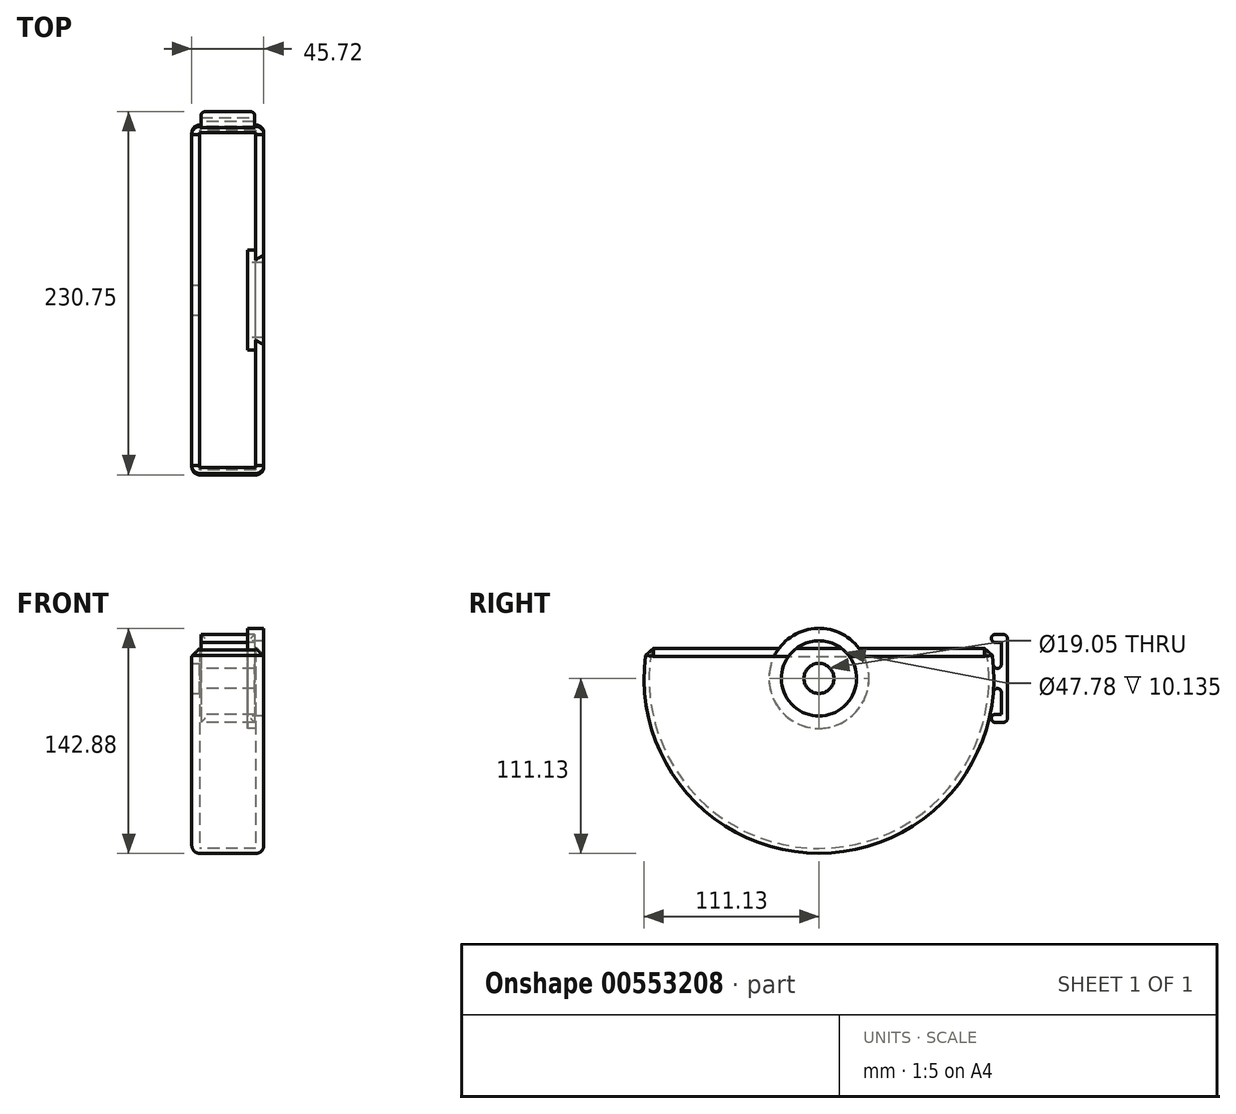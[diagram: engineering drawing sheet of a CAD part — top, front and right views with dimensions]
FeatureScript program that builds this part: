
annotation { "Feature Type Name" : "Feature", "Feature Type Description" : "" }
export const myFeature = defineFeature(function(context is Context, id is Id, definition is map)
    precondition{}
    {
        {
            var Q0;
            Q0=qCreatedBy(makeId("Right.planeOp"),FACE);
            var sketch = newSketch(context, id + "F0", { "sketchPlane" : qUnion([Q0])});
            skCircle(sketch, "E0", {"center": v(0, 0) * mm, "radius": 9.52 * mm});
            skSolve(sketch);
        }
        {
            var Q0;
            Q0=qCreatedBy(makeId("Right.planeOp"),FACE);
            var sketch = newSketch(context, id + "F1", { "sketchPlane" : qUnion([Q0])});
            skCircle(sketch, "E1", {"center": v(0, 0) * mm, "radius": 111.13 * mm});
            skCircle(sketch, "E2", {"center": v(0, 0) * mm, "radius": 107.95 * mm});
            skSolve(sketch);
        }
        {
            var Q0;
            Q0 = qSketchRegion(id + "F1", true);
            extrude(context, id + "F2", {"entities" : qUnion([Q0]), "endBound" : BoundingType.SYMMETRIC, "depth" : 35.56 * mm, "offsetDistance" : 25.4 * mm});
        }
        {
            var Q0;
            Q0=qCreatedBy(makeId("Right.planeOp"),FACE);
            cPlane(context, id + "F3", {"entities" : qUnion([Q0]), "cplaneType" : CPlaneType.OFFSET, "offset" : 17.78 * mm, "width" : 152.4 * mm, "height" : 152.4 * mm});
        }
        {
            var Q0;
            Q0=qCreatedBy(makeId("Right.planeOp"),FACE);
            cPlane(context, id + "F4", {"entities" : qUnion([Q0]), "cplaneType" : CPlaneType.OFFSET, "offset" : 17.78 * mm, "oppositeDirection" : true, "width" : 152.4 * mm, "height" : 152.4 * mm});
        }
        {
            var Q0;
            Q0=qCreatedBy(id+"F3.planeOp",FACE);
            var sketch = newSketch(context, id + "F5", { "sketchPlane" : qUnion([Q0])});
            skCircle(sketch, "E3", {"center": v(0, 0) * mm, "radius": 111.13 * mm});
            skSolve(sketch);
        }
        {
            var Q0;
            Q0 = qSketchRegion(id + "F5", true);
            extrude(context, id + "F6", {"entities" : qUnion([Q0]), "operationType" : NewBodyOperationType.ADD, "depth" : 5.08 * mm, "offsetDistance" : 25.4 * mm});
        }
        {
            var Q0;
            Q0=qCreatedBy(id+"F4.planeOp",FACE);
            var sketch = newSketch(context, id + "F7", { "sketchPlane" : qUnion([Q0])});
            skCircle(sketch, "E4", {"center": v(0, 0) * mm, "radius": 111.13 * mm});
            skSolve(sketch);
        }
        {
            var Q0;
            Q0 = qSketchRegion(id + "F7", true);
            extrude(context, id + "F8", {"entities" : qUnion([Q0]), "operationType" : NewBodyOperationType.ADD, "oppositeDirection" : true, "depth" : 5.08 * mm, "offsetDistance" : 25.4 * mm});
        }
        {
            var Q0;
            Q0=qCreatedBy(makeId("Right.planeOp"),FACE);
            var sketch = newSketch(context, id + "F9", { "sketchPlane" : qUnion([Q0])});
            skLineSegment(sketch, "E5.bottom", {"start": v(-117, 19.1) * mm, "end": v(123.15, 19.1) * mm});
            skLineSegment(sketch, "E5.top", {"start": v(-117, 115.3) * mm, "end": v(123.15, 115.3) * mm});
            skLineSegment(sketch, "E5.left", {"start": v(-117, 19.1) * mm, "end": v(-117, 115.3) * mm});
            skLineSegment(sketch, "E5.right", {"start": v(123.15, 19.1) * mm, "end": v(123.15, 115.3) * mm});
            skSolve(sketch);
        }
        {
            var Q0;
            Q0 = qSketchRegion(id + "F9", true);
            extrude(context, id + "F10", {"entities" : qUnion([Q0]), "operationType" : NewBodyOperationType.REMOVE, "endBound" : BoundingType.SYMMETRIC, "depth" : 76.2 * mm, "offsetDistance" : 25.4 * mm});
        }
        {
            var Q0;
            Q0 = qSketchRegion(id + "F0", true);
            extrude(context, id + "F11", {"entities" : qUnion([Q0]), "operationType" : NewBodyOperationType.REMOVE, "endBound" : BoundingType.SYMMETRIC, "oppositeDirection" : true, "depth" : 76.2 * mm, "offsetDistance" : 25.4 * mm});
        }
        {
            var Q0;
            Q0=makeQuery(id+"F8.opExtrude","CAP_EDGE",EDGE,{"disambiguationData":[OSD([sQuery(id+"F7.wireOp",EDGE,"E4")])],"isStart":false});
            var Q1;
            Q1=makeQuery(id+"F6.opExtrude","CAP_EDGE",EDGE,{"disambiguationData":[OSD([sQuery(id+"F5.wireOp",EDGE,"E3")])],"isStart":false});
            var Q2;
            Q2=makeQuery(id+"F2.opExtrude","CAP_EDGE",EDGE,{"disambiguationData":[OSD([sQuery(id+"F1.wireOp",EDGE,"E2")])],"isStart":true});
            var Q3;
            Q3=makeQuery(id+"F2.opExtrude","CAP_EDGE",EDGE,{"disambiguationData":[OSD([sQuery(id+"F1.wireOp",EDGE,"E2")])],"isStart":false});
            fillet(context, id + "F12", {"entities" : qUnion([Q0, Q1, Q2, Q3]), "radius" : 5.08 * mm, "tangentPropagation" : true, "allowEdgeOverflow" : false});
        }
        {
            var Q0;
            Q0=qCreatedBy(makeId("Right.planeOp"),FACE);
            var sketch = newSketch(context, id + "F13", { "sketchPlane" : qUnion([Q0])});
            skLineSegment(sketch, "E6.bottom", {"start": v(119.62, 27.94) * mm, "end": v(115.81, 27.94) * mm});
            skLineSegment(sketch, "E6.top", {"start": v(119.62, -27.94) * mm, "end": v(115.81, -27.94) * mm});
            skLineSegment(sketch, "E6.left", {"start": v(119.62, 27.94) * mm, "end": v(119.62, -27.94) * mm});
            skLineSegment(sketch, "E6.right", {"start": v(115.81, 27.94) * mm, "end": v(115.81, -27.94) * mm});
            skPoint(sketch, "E6.middle", {"position": v(117.72, 0) * mm});
            skLineSegment(sketch, "E7.bottom", {"start": v(110.33, -1.9) * mm, "end": v(119.12, -1.9) * mm});
            skLineSegment(sketch, "E7.top", {"start": v(110.33, 1.9) * mm, "end": v(119.12, 1.9) * mm});
            skLineSegment(sketch, "E7.left", {"start": v(110.33, -1.9) * mm, "end": v(110.33, 1.9) * mm});
            skLineSegment(sketch, "E7.right", {"start": v(119.12, -1.9) * mm, "end": v(119.12, 1.9) * mm});
            skLineSegment(sketch, "E8.bottom", {"start": v(115.81, 27.94) * mm, "end": v(109.46, 27.94) * mm});
            skLineSegment(sketch, "E8.top", {"start": v(115.81, 22.86) * mm, "end": v(109.46, 22.86) * mm});
            skLineSegment(sketch, "E8.left", {"start": v(115.81, 27.94) * mm, "end": v(115.81, 22.86) * mm});
            skLineSegment(sketch, "E8.right", {"start": v(109.46, 27.94) * mm, "end": v(109.46, 22.86) * mm});
            skLineSegment(sketch, "E9.bottom", {"start": v(115.81, -27.94) * mm, "end": v(109.46, -27.94) * mm});
            skLineSegment(sketch, "E9.top", {"start": v(115.81, -22.86) * mm, "end": v(109.46, -22.86) * mm});
            skLineSegment(sketch, "E9.left", {"start": v(115.81, -27.94) * mm, "end": v(115.81, -22.86) * mm});
            skLineSegment(sketch, "E9.right", {"start": v(109.46, -27.94) * mm, "end": v(109.46, -22.86) * mm});
            skSolve(sketch);
        }
        {
            var Q0;
            Q0 = qSketchRegion(id + "F13", true);
            extrude(context, id + "F14", {"entities" : qUnion([Q0]), "operationType" : NewBodyOperationType.ADD, "endBound" : BoundingType.SYMMETRIC, "depth" : 34.04 * mm, "offsetDistance" : 25.4 * mm});
        }
        {
            var Q0;
            Q0=makeQuery(id+"F14.boolean.opBoolean","INTERSECT",EDGE,{"derivedFrom":[makeQuery(id+"F8.boolean.opBoolean","MERGE",FACE,{"derivedFrom":[makeQuery(id+"F6.boolean.opBoolean","MERGE",FACE,{"derivedFrom":[makeQuery(id+"F2.opExtrude","SWEPT_FACE",FACE,{"disambiguationData":[OSD([sQuery(id+"F1.wireOp",EDGE,"E1")])]}),makeQuery(id+"F6.opExtrude","SWEPT_FACE",FACE,{"disambiguationData":[OSD([sQuery(id+"F5.wireOp",EDGE,"E3")])]})]}),makeQuery(id+"F8.opExtrude","SWEPT_FACE",FACE,{"disambiguationData":[OSD([sQuery(id+"F7.wireOp",EDGE,"E4")])]})]}),makeQuery(id+"F14.opExtrude","SWEPT_FACE",FACE,{"disambiguationData":[OSD([sQuery(id+"F13.wireOp",EDGE,"E7.top")])]})]});
            var Q1;
            Q1=makeQuery(id+"F14.boolean.opBoolean","INTERSECT",EDGE,{"derivedFrom":[makeQuery(id+"F8.boolean.opBoolean","MERGE",FACE,{"derivedFrom":[makeQuery(id+"F6.boolean.opBoolean","MERGE",FACE,{"derivedFrom":[makeQuery(id+"F2.opExtrude","SWEPT_FACE",FACE,{"disambiguationData":[OSD([sQuery(id+"F1.wireOp",EDGE,"E1")])]}),makeQuery(id+"F6.opExtrude","SWEPT_FACE",FACE,{"disambiguationData":[OSD([sQuery(id+"F5.wireOp",EDGE,"E3")])]})]}),makeQuery(id+"F8.opExtrude","SWEPT_FACE",FACE,{"disambiguationData":[OSD([sQuery(id+"F7.wireOp",EDGE,"E4")])]})]}),makeQuery(id+"F14.opExtrude","SWEPT_FACE",FACE,{"disambiguationData":[OSD([sQuery(id+"F13.wireOp",EDGE,"E7.bottom")])]})]});
            var Q2;
            Q2=makeQuery(id+"F14.opExtrude","SWEPT_EDGE",EDGE,{"disambiguationData":[OSD([sQuery(id+"F13.wireOp",EDGE,"E8.top"),sQuery(id+"F13.wireOp",EDGE,"E8.right")])]});
            var Q3;
            Q3=makeQuery(id+"F14.opExtrude","SWEPT_EDGE",EDGE,{"disambiguationData":[OSD([sQuery(id+"F13.wireOp",EDGE,"E9.bottom"),sQuery(id+"F13.wireOp",EDGE,"E9.right")])]});
            var Q4;
            Q4=makeQuery(id+"F14.opExtrude","SWEPT_EDGE",EDGE,{"disambiguationData":[OSD([sQuery(id+"F13.wireOp",EDGE,"E8.bottom"),sQuery(id+"F13.wireOp",EDGE,"E8.right")])]});
            var Q5;
            Q5=makeQuery(id+"F14.opExtrude","SWEPT_EDGE",EDGE,{"disambiguationData":[OSD([sQuery(id+"F13.wireOp",EDGE,"E9.top"),sQuery(id+"F13.wireOp",EDGE,"E9.right")])]});
            var Q6;
            Q6=makeQuery(id+"F14.opExtrude","SWEPT_EDGE",EDGE,{"disambiguationData":[OSD([sQuery(id+"F13.wireOp",EDGE,"E6.bottom"),sQuery(id+"F13.wireOp",EDGE,"E6.left")])]});
            var Q7;
            Q7=makeQuery(id+"F14.opExtrude","CAP_EDGE",EDGE,{"disambiguationData":[OSD([sQuery(id+"F13.wireOp",EDGE,"E6.left")])],"isStart":false});
            var Q8;
            Q8=makeQuery(id+"F14.opExtrude","CAP_EDGE",EDGE,{"disambiguationData":[OSD([sQuery(id+"F13.wireOp",EDGE,"E6.left")])],"isStart":true});
            var Q9;
            Q9=makeQuery(id+"F14.opExtrude","SWEPT_EDGE",EDGE,{"disambiguationData":[OSD([sQuery(id+"F13.wireOp",EDGE,"E6.top"),sQuery(id+"F13.wireOp",EDGE,"E6.left")])]});
            var Q10;
            Q10=makeQuery(id+"F14.opExtrude","SWEPT_EDGE",EDGE,{"disambiguationData":[OSD([sQuery(id+"F13.wireOp",EDGE,"E6.right"),sQuery(id+"F13.wireOp",EDGE,"E7.top")])]});
            var Q11;
            Q11=makeQuery(id+"F14.opExtrude","SWEPT_EDGE",EDGE,{"disambiguationData":[OSD([sQuery(id+"F13.wireOp",EDGE,"E6.right"),sQuery(id+"F13.wireOp",EDGE,"E7.bottom")])]});
            fillet(context, id + "F15", {"entities" : qUnion([Q0, Q1, Q2, Q3, Q4, Q5, Q6, Q7, Q8, Q9, Q10, Q11]), "radius" : 2.54 * mm, "tangentPropagation" : true, "allowEdgeOverflow" : false});
        }
        {
            var Q0;
            Q0=qCreatedBy(id+"F3.planeOp",FACE);
            var sketch = newSketch(context, id + "F16", { "sketchPlane" : qUnion([Q0])});
            skCircle(sketch, "E10", {"center": v(0, 0) * mm, "radius": 31.75 * mm});
            skSolve(sketch);
        }
        {
            var Q0;
            Q0 = qSketchRegion(id + "F16", true);
            extrude(context, id + "F17", {"entities" : qUnion([Q0]), "operationType" : NewBodyOperationType.ADD, "endBound" : BoundingType.SYMMETRIC, "depth" : 10.1 * mm, "offsetDistance" : 25.4 * mm});
        }
        {
            var Q0;
            Q0=qCreatedBy(makeId("Right.planeOp"),FACE);
            var sketch = newSketch(context, id + "F18", { "sketchPlane" : qUnion([Q0])});
            skCircle(sketch, "E11", {"center": v(0, 0) * mm, "radius": 23.89 * mm});
            skSolve(sketch);
        }
        {
            var Q0;
            Q0 = qSketchRegion(id + "F18", true);
            extrude(context, id + "F19", {"entities" : qUnion([Q0]), "operationType" : NewBodyOperationType.REMOVE, "depth" : 50.8 * mm, "offsetDistance" : 25.4 * mm});
        }
        {
            var Q0;
            Q0=qCreatedBy(makeId("Right.planeOp"),FACE);
            var sketch = newSketch(context, id + "F20", { "sketchPlane" : qUnion([Q0])});
            skLineSegment(sketch, "E12.bottom", {"start": v(116.97, 6.35) * mm, "end": v(110, 6.35) * mm});
            skLineSegment(sketch, "E12.top", {"start": v(116.97, -6.35) * mm, "end": v(110, -6.35) * mm});
            skLineSegment(sketch, "E12.left", {"start": v(116.97, 6.35) * mm, "end": v(116.97, -6.35) * mm});
            skLineSegment(sketch, "E12.right", {"start": v(110, 6.35) * mm, "end": v(110, -6.35) * mm});
            skPoint(sketch, "E12.middle", {"position": v(113.49, 0) * mm});
            skSolve(sketch);
        }
        {
            var Q0;
            Q0 = qSketchRegion(id + "F20", true);
            extrude(context, id + "F21", {"entities" : qUnion([Q0]), "operationType" : NewBodyOperationType.ADD, "endBound" : BoundingType.SYMMETRIC, "oppositeDirection" : true, "depth" : 34.04 * mm, "offsetDistance" : 25.4 * mm});
        }
        {
            var Q0;
            Q0=makeQuery(id+"F21.boolean.opBoolean","INTERSECT",EDGE,{"derivedFrom":[makeQuery(id+"F8.boolean.opBoolean","MERGE",FACE,{"derivedFrom":[makeQuery(id+"F6.boolean.opBoolean","MERGE",FACE,{"derivedFrom":[makeQuery(id+"F2.opExtrude","SWEPT_FACE",FACE,{"disambiguationData":[OSD([sQuery(id+"F1.wireOp",EDGE,"E1")])]}),makeQuery(id+"F6.opExtrude","SWEPT_FACE",FACE,{"disambiguationData":[OSD([sQuery(id+"F5.wireOp",EDGE,"E3")])]})]}),makeQuery(id+"F8.opExtrude","SWEPT_FACE",FACE,{"disambiguationData":[OSD([sQuery(id+"F7.wireOp",EDGE,"E4")])]})]}),makeQuery(id+"F21.opExtrude","SWEPT_FACE",FACE,{"disambiguationData":[OSD([sQuery(id+"F20.wireOp",EDGE,"E12.bottom")])]})]});
            var Q1;
            {var subQ0=sQuery(id+"F13.wireOp",EDGE,"E6.right");Q1=makeQuery(id+"F21.boolean.opBoolean","INTERSECT",EDGE,{"derivedFrom":[makeQuery(id+"F14.opExtrude","SWEPT_FACE",FACE,{"disambiguationData":[OSD([subQ0]),TDD([makeQuery(id+"F13.imprint","IMPRINT",EDGE,{"disambiguationData":[TD([[makeQuery(id+"F13.imprint","INTERSECT",VERTEX,{"derivedFrom":[subQ0,sQuery(id+"F13.wireOp",EDGE,"E7.top")]}),1.0]])],"derivedFrom":subQ0})])]}),makeQuery(id+"F21.opExtrude","SWEPT_FACE",FACE,{"disambiguationData":[OSD([sQuery(id+"F20.wireOp",EDGE,"E12.bottom")])]})]});}
            var Q2;
            Q2=makeQuery(id+"F21.boolean.opBoolean","INTERSECT",EDGE,{"derivedFrom":[makeQuery(id+"F8.boolean.opBoolean","MERGE",FACE,{"derivedFrom":[makeQuery(id+"F6.boolean.opBoolean","MERGE",FACE,{"derivedFrom":[makeQuery(id+"F2.opExtrude","SWEPT_FACE",FACE,{"disambiguationData":[OSD([sQuery(id+"F1.wireOp",EDGE,"E1")])]}),makeQuery(id+"F6.opExtrude","SWEPT_FACE",FACE,{"disambiguationData":[OSD([sQuery(id+"F5.wireOp",EDGE,"E3")])]})]}),makeQuery(id+"F8.opExtrude","SWEPT_FACE",FACE,{"disambiguationData":[OSD([sQuery(id+"F7.wireOp",EDGE,"E4")])]})]}),makeQuery(id+"F21.opExtrude","SWEPT_FACE",FACE,{"disambiguationData":[OSD([sQuery(id+"F20.wireOp",EDGE,"E12.top")])]})]});
            var Q3;
            {var subQ0=sQuery(id+"F13.wireOp",EDGE,"E6.right");Q3=makeQuery(id+"F21.boolean.opBoolean","INTERSECT",EDGE,{"derivedFrom":[makeQuery(id+"F14.opExtrude","SWEPT_FACE",FACE,{"disambiguationData":[OSD([subQ0]),TDD([makeQuery(id+"F13.imprint","IMPRINT",EDGE,{"disambiguationData":[TD([[makeQuery(id+"F13.imprint","INTERSECT",VERTEX,{"derivedFrom":[subQ0,sQuery(id+"F13.wireOp",EDGE,"E7.bottom")]}),-1.0]])],"derivedFrom":subQ0})])]}),makeQuery(id+"F21.opExtrude","SWEPT_FACE",FACE,{"disambiguationData":[OSD([sQuery(id+"F20.wireOp",EDGE,"E12.top")])]})]});}
            fillet(context, id + "F22", {"entities" : qUnion([Q0, Q1, Q2, Q3]), "radius" : 2.54 * mm, "tangentPropagation" : true, "allowEdgeOverflow" : false});
        }
        {
            var Q0;
            Q0=makeQuery(id+"F10.boolean.opBoolean","INTERSECT",EDGE,{"derivedFrom":[makeQuery(id+"F8.opExtrude","CAP_FACE",FACE,{"disambiguationData":[OSD([sQuery(id+"F7.wireOp",EDGE,"E4")])],"isStart":false}),makeQuery(id+"F10.opExtrude","SWEPT_FACE",FACE,{"disambiguationData":[OSD([sQuery(id+"F9.wireOp",EDGE,"E5.bottom")])]})]});
            var Q1;
            Q1=makeQuery(id+"F12.opFillet","BLEND_EDGE",EDGE,{"disambiguationData":[OD(0.0)],"blendedFrom":[makeQuery(id+"F8.opExtrude","CAP_EDGE",EDGE,{"disambiguationData":[OSD([sQuery(id+"F7.wireOp",EDGE,"E4")])],"isStart":false}),makeQuery(id+"F10.boolean.opBoolean","COPY",FACE,{"derivedFrom":makeQuery(id+"F10.opExtrude","SWEPT_FACE",FACE,{"disambiguationData":[OSD([sQuery(id+"F9.wireOp",EDGE,"E5.bottom")])]})})],"blendedInto":[makeQuery(id+"F10.boolean.opBoolean","COPY",FACE,{"derivedFrom":makeQuery(id+"F10.opExtrude","SWEPT_FACE",FACE,{"disambiguationData":[OSD([sQuery(id+"F9.wireOp",EDGE,"E5.bottom")])]})})]});
            var Q2;
            Q2=makeQuery(id+"F10.boolean.opBoolean","INTERSECT",EDGE,{"disambiguationData":[OD(0.0)],"derivedFrom":[makeQuery(id+"F8.boolean.opBoolean","MERGE",FACE,{"derivedFrom":[makeQuery(id+"F6.boolean.opBoolean","MERGE",FACE,{"derivedFrom":[makeQuery(id+"F2.opExtrude","SWEPT_FACE",FACE,{"disambiguationData":[OSD([sQuery(id+"F1.wireOp",EDGE,"E1")])]}),makeQuery(id+"F6.opExtrude","SWEPT_FACE",FACE,{"disambiguationData":[OSD([sQuery(id+"F5.wireOp",EDGE,"E3")])]})]}),makeQuery(id+"F8.opExtrude","SWEPT_FACE",FACE,{"disambiguationData":[OSD([sQuery(id+"F7.wireOp",EDGE,"E4")])]})]}),makeQuery(id+"F10.opExtrude","SWEPT_FACE",FACE,{"disambiguationData":[OSD([sQuery(id+"F9.wireOp",EDGE,"E5.bottom")])]})]});
            var Q3;
            Q3=makeQuery(id+"F12.opFillet","BLEND_EDGE",EDGE,{"disambiguationData":[OD(0.0)],"blendedFrom":[makeQuery(id+"F6.opExtrude","CAP_EDGE",EDGE,{"disambiguationData":[OSD([sQuery(id+"F5.wireOp",EDGE,"E3")])],"isStart":false}),makeQuery(id+"F10.boolean.opBoolean","COPY",FACE,{"derivedFrom":makeQuery(id+"F10.opExtrude","SWEPT_FACE",FACE,{"disambiguationData":[OSD([sQuery(id+"F9.wireOp",EDGE,"E5.bottom")])]})})],"blendedInto":[makeQuery(id+"F10.boolean.opBoolean","COPY",FACE,{"derivedFrom":makeQuery(id+"F10.opExtrude","SWEPT_FACE",FACE,{"disambiguationData":[OSD([sQuery(id+"F9.wireOp",EDGE,"E5.bottom")])]})})]});
            var Q4;
            Q4=makeQuery(id+"F19.boolean.opBoolean","SPLIT",EDGE,{"disambiguationData":[OD(0.0)],"derivedFrom":makeQuery(id+"F10.boolean.opBoolean","INTERSECT",EDGE,{"derivedFrom":[makeQuery(id+"F6.opExtrude","CAP_FACE",FACE,{"disambiguationData":[OSD([sQuery(id+"F5.wireOp",EDGE,"E3")])],"isStart":false}),makeQuery(id+"F10.opExtrude","SWEPT_FACE",FACE,{"disambiguationData":[OSD([sQuery(id+"F9.wireOp",EDGE,"E5.bottom")])]})]})});
            chamfer(context, id + "F23", {"entities" : qUnion([Q0, Q1, Q2, Q3, Q4]), "width" : 5.08 * mm, "tangentPropagation" : true});
        }
    });
